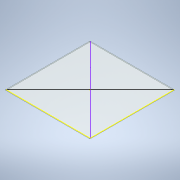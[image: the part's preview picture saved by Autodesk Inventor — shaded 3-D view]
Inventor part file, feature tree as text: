
AUTODESK INVENTOR PART (.ipt)
format: ipt  version: 2020 (Build 240168000, 168)  size: 99,840 bytes
history: native  units: mm
features: sketch x2, other x1, extrude x1
ambient origin geometry x8: Origin, YZ Plane, XZ Plane, XY Plane, X Axis, Y Axis, Z Axis, Center Point
bodies: Body1 (feature_tree)
feature tree (4):
  other  "Bryła1"
  extrude  "Wyciągnięcie proste1"  Depth=100.0mm
  sketch  "Szkic2"
  sketch  "Szkic1"
